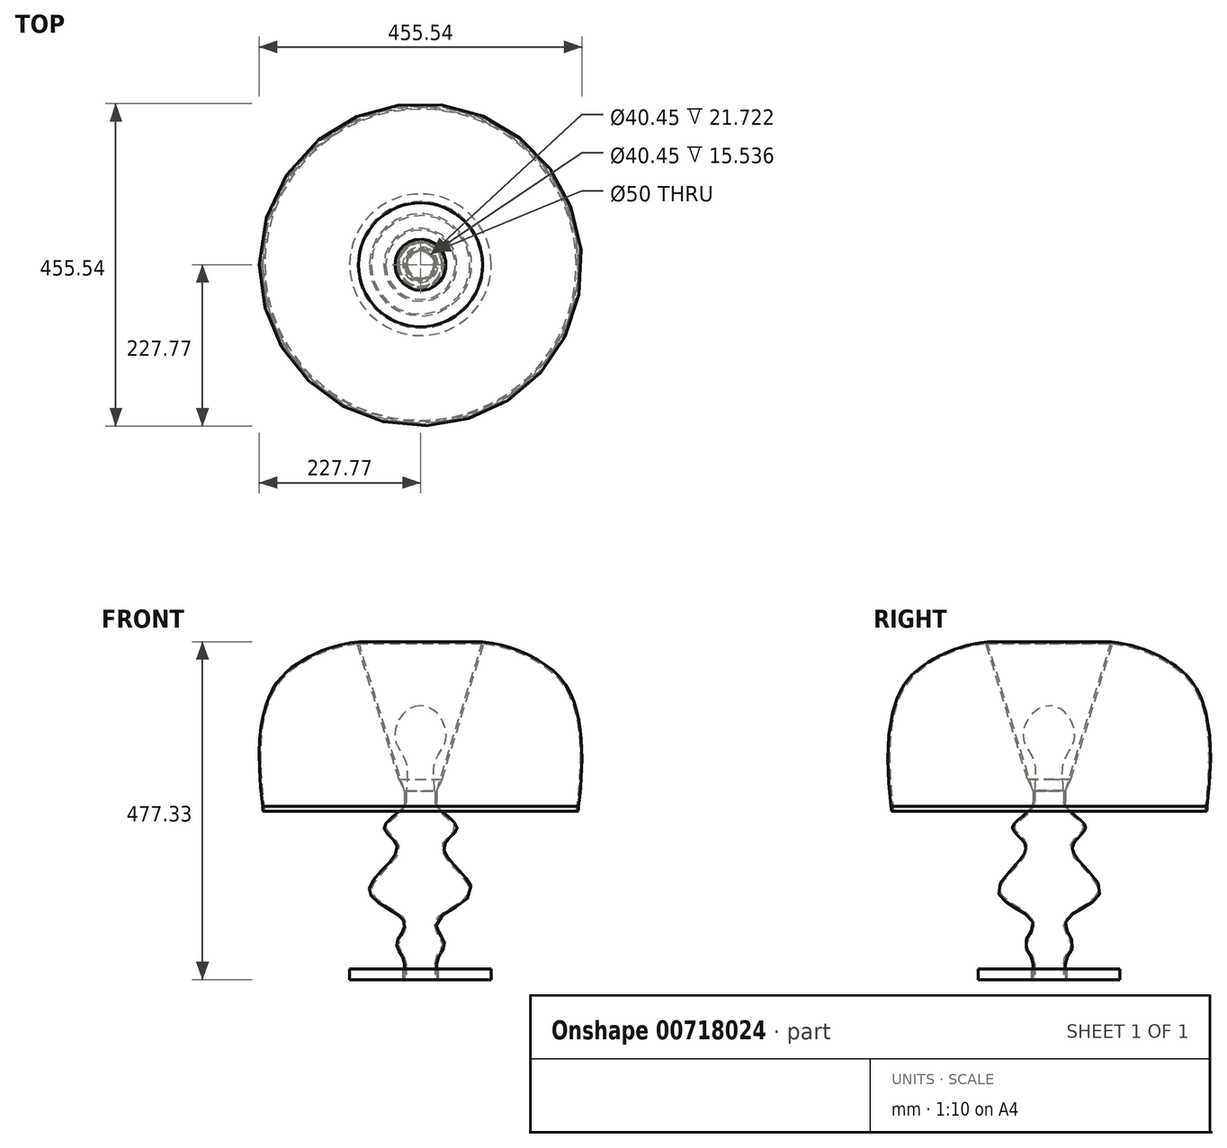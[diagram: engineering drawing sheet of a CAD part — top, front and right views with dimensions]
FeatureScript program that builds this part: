
annotation { "Feature Type Name" : "Feature", "Feature Type Description" : "" }
export const myFeature = defineFeature(function(context is Context, id is Id, definition is map)
    precondition{}
    {
        {
            var Q0;
            Q0=qCreatedBy(makeId("Front.planeOp"),FACE);
            var sketch = newSketch(context, id + "F0", { "sketchPlane" : qUnion([Q0])});
            skLineSegment(sketch, "E0.bottom", {"start": v(-25, 15) * mm, "end": v(-100, 15) * mm});
            skLineSegment(sketch, "E0.top", {"start": v(-25, 0) * mm, "end": v(-100, 0) * mm});
            skLineSegment(sketch, "E0.left", {"start": v(-25, 15) * mm, "end": v(-25, 0) * mm});
            skLineSegment(sketch, "E0.right", {"start": v(-100, 15) * mm, "end": v(-100, 0) * mm});
            skLineSegment(sketch, "E1", {"start": v(0, 0) * mm, "end": v(0, 57.1) * mm, "construction": true});
            skSolve(sketch);
        }
        {
            var Q0;
            Q0 = qSketchRegion(id + "F0", true);
            var Q1;
            Q1=sQuery(id+"F0.wireOp",EDGE,"E1");
            revolve(context, id + "F1", {"surfaceOperationType" : NewSurfaceOperationType.NEW, "entities" : qUnion([Q0]), "axis" : qUnion([Q1]), "revolveType" : RevolveType.FULL});
        }
        {
            var Q0;
            Q0=qCreatedBy(makeId("Front.planeOp"),FACE);
            var sketch = newSketch(context, id + "F2", { "sketchPlane" : qUnion([Q0])});
            skLineSegment(sketch, "E2", {"start": v(-22.73, 0) * mm, "end": v(-22.73, 21.72) * mm});
            skLineSegment(sketch, "E3", {"start": v(-22.73, 0) * mm, "end": v(0, 0) * mm});
            skLineSegment(sketch, "E4", {"start": v(0, 0) * mm, "end": v(0, 266.25) * mm});
            skLineSegment(sketch, "E5", {"start": v(0, 266.25) * mm, "end": v(-22.73, 266.25) * mm});
            skLineSegment(sketch, "E6", {"start": v(-22.73, 266.25) * mm, "end": v(-22.73, 250.71) * mm});
            skFitSpline(sketch, "E7", {"points": [v(-22.73, 250.71) * mm, v(-51.67, 215.5) * mm, v(-32.68, 185.8) * mm, v(-72.24, 124.81) * mm, v(-22.73, 81.45) * mm, v(-33.95, 50.46) * mm, v(-22.73, 21.72) * mm], "startDerivative": vector(0, -247.16) * mm, "endDerivative": vector(0, -282.5) * mm});
            skSolve(sketch);
        }
        {
            var Q0;
            Q0=makeQuery(id+"F2.imprint","IMPRINT",FACE,{"disambiguationData":[TD([[makeQuery(id+"F2.imprint","IMPRINT",EDGE,{"derivedFrom":sQuery(id+"F2.wireOp",EDGE,"E2")}),-1.0]])]});
            var Q1;
            Q1=sQuery(id+"F2.wireOp",EDGE,"E4");
            revolve(context, id + "F3", {"surfaceOperationType" : NewSurfaceOperationType.NEW, "entities" : qUnion([Q0]), "axis" : qUnion([Q1]), "revolveType" : RevolveType.FULL});
        }
        {
            var Q0;
            Q0=makeQuery(id+"F3.opRevolve","SWEPT_FACE",FACE,{"disambiguationData":[OSD([sQuery(id+"F2.wireOp",EDGE,"E5")])]});
            var Q1;
            Q1=makeQuery(id+"F3.opRevolve","SWEPT_FACE",FACE,{"disambiguationData":[OSD([sQuery(id+"F2.wireOp",EDGE,"E3")])]});
            shell(context, id + "F4", {"entities" : qUnion([Q0, Q1]), "thickness" : 2.5 * mm});
        }
        {
            var Q0;
            Q0=qCreatedBy(makeId("Front.planeOp"),FACE);
            var sketch = newSketch(context, id + "F5", { "sketchPlane" : qUnion([Q0])});
            skFitSpline(sketch, "E8", {"points": [v(-223.1, 244.84) * mm, v(-179.21, 298.82) * mm, v(-139.42, 244.84) * mm, v(-121.42, 296.85) * mm, v(-22.73, 266.25) * mm], "startDerivative": vector(-2.8, -372.4) * mm, "endDerivative": vector(265.83, -684.37) * mm});
            skLineSegment(sketch, "E9", {"start": v(0, 0) * mm, "end": v(0, 486.67) * mm});
            skFitSpline(sketch, "E10", {"points": [v(-223.1, 244.84) * mm, v(-164.82, 452.04) * mm, v(-25.61, 477.63) * mm], "startDerivative": vector(-94.63, 794.34) * mm, "endDerivative": vector(444.03, -35.77) * mm});
            skPoint(sketch, "E11.endSnap0", {"position": v(-24.17, 371.94) * mm});
            skLineSegment(sketch, "E12", {"start": v(-22.73, 266.25) * mm, "end": v(-87.49, 477.33) * mm});
            skSolve(sketch);
        }
        {
            var Q0;
            Q0=makeQuery(id+"F5.imprint","IMPRINT",FACE,{"disambiguationData":[TD([[makeQuery(id+"F5.imprint","IMPRINT",EDGE,{"derivedFrom":sQuery(id+"F5.wireOp",EDGE,"E8")}),1.0]])]});
            var Q1;
            Q1=sQuery(id+"F5.wireOp",EDGE,"E9");
            revolve(context, id + "F6", {"surfaceOperationType" : NewSurfaceOperationType.NEW, "entities" : qUnion([Q0]), "axis" : qUnion([Q1]), "revolveType" : RevolveType.FULL});
        }
        {
            var Q0;
            Q0=makeQuery(id+"F6.opRevolve","SWEPT_FACE",FACE,{"disambiguationData":[OSD([sQuery(id+"F5.wireOp",EDGE,"E8")])]});
            shell(context, id + "F7", {"entities" : qUnion([Q0]), "thickness" : 2.5 * mm});
        }
        {
            var Q0;
            Q0=qCreatedBy(makeId("Front.planeOp"),FACE);
            var sketch = newSketch(context, id + "F8", { "sketchPlane" : qUnion([Q0])});
            skLineSegment(sketch, "E13", {"start": v(0, 0) * mm, "end": v(0, 93.7) * mm, "construction": true});
            skSolve(sketch);
        }
        {
            var Q0;
            Q0=qCreatedBy(makeId("Front.planeOp"),FACE);
            var sketch = newSketch(context, id + "F9", { "sketchPlane" : qUnion([Q0])});
            skLineSegment(sketch, "E14", {"start": v(0, 267) * mm, "end": v(0, 387) * mm});
            skLineSegment(sketch, "E15", {"start": v(0, 387) * mm, "end": v(48.68, 387) * mm, "construction": true});
            skLineSegment(sketch, "E16", {"start": v(-20, 267) * mm, "end": v(-20, 228.91) * mm, "construction": true});
            skFitSpline(sketch, "E17", {"points": [v(0, 387) * mm, v(-36.08, 343.07) * mm, v(-20.52, 307.25) * mm, v(-20, 267) * mm], "startDerivative": vector(-190.6, 0) * mm, "endDerivative": vector(0, -99.84) * mm});
            skLineSegment(sketch, "E18", {"start": v(-20, 267) * mm, "end": v(0, 267) * mm});
            skSolve(sketch);
        }
        {
            var Q0;
            Q0 = qSketchRegion(id + "F9", true);
            var Q1;
            Q1=sQuery(id+"F9.wireOp",EDGE,"E14");
            revolve(context, id + "F10", {"surfaceOperationType" : NewSurfaceOperationType.NEW, "entities" : qUnion([Q0]), "axis" : qUnion([Q1]), "revolveType" : RevolveType.FULL});
        }
    });
